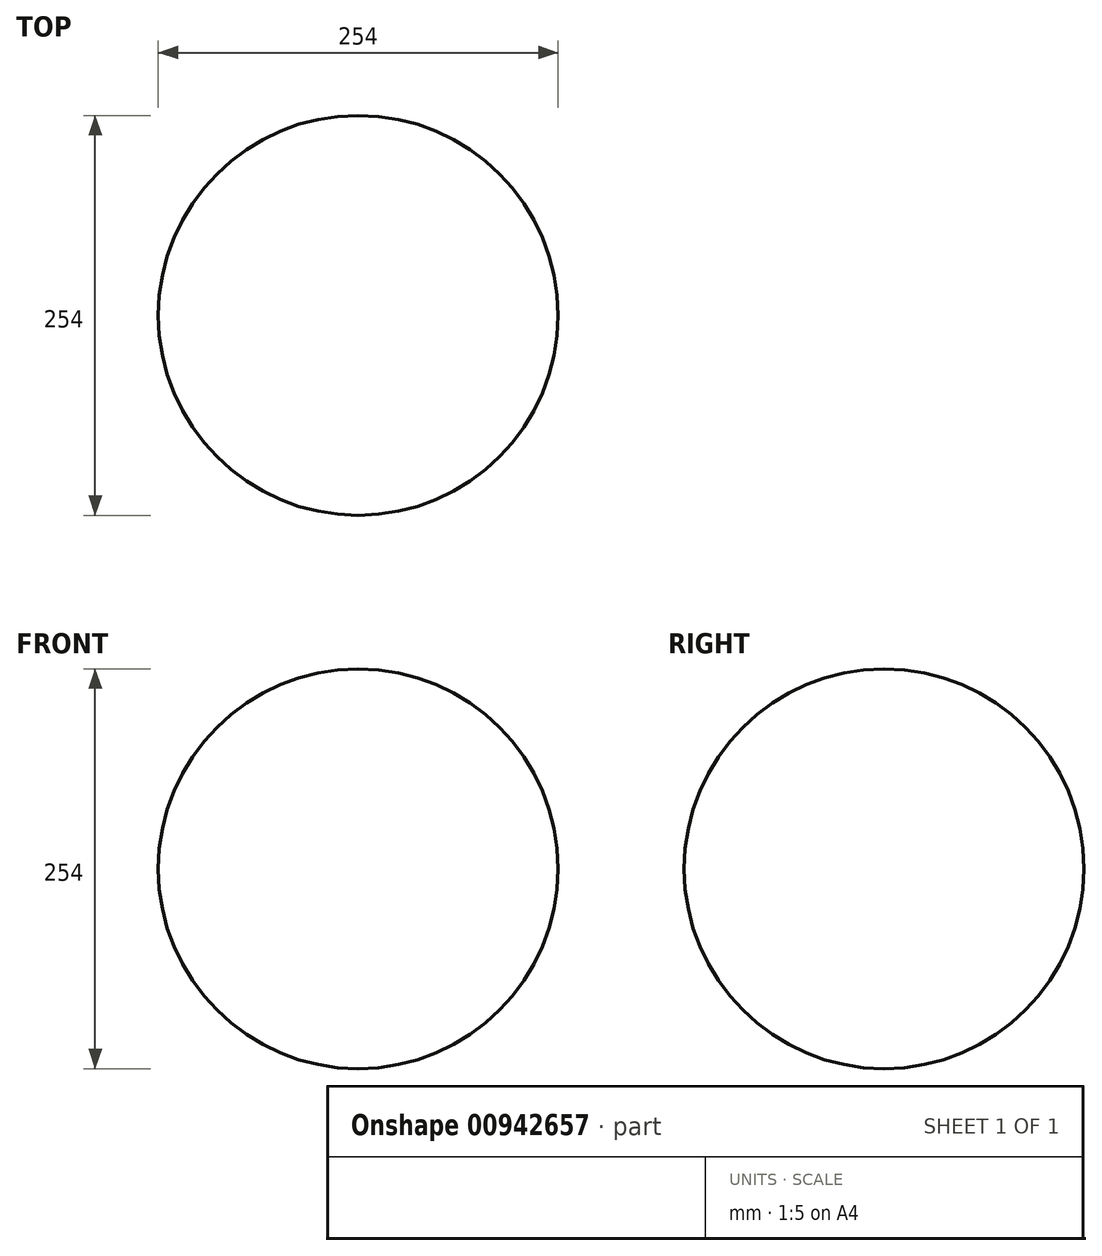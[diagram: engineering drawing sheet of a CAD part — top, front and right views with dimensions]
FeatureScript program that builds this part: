
annotation { "Feature Type Name" : "Feature", "Feature Type Description" : "" }
export const myFeature = defineFeature(function(context is Context, id is Id, definition is map)
    precondition{}
    {
        {
            var Q0;
            Q0=qCreatedBy(makeId("Right.planeOp"),FACE);
            var sketch = newSketch(context, id + "F0", { "sketchPlane" : qUnion([Q0])});
            skLineSegment(sketch, "E0", {"start": v(0, 127) * mm, "end": v(0, -127) * mm});
            skArc(sketch, "E1", {"start": v(0, -127) * mm, "mid": v(127, 0) * mm, "end": v(0, 127) * mm});
            skSolve(sketch);
        }
        {
            var Q0;
            Q0=makeQuery(id+"F0.imprint","IMPRINT",FACE,{"disambiguationData":[TD([[makeQuery(id+"F0.imprint","IMPRINT",EDGE,{"derivedFrom":sQuery(id+"F0.wireOp",EDGE,"E0")}),1.0]])]});
            var Q1;
            Q1=sQuery(id+"F0.wireOp",EDGE,"E0");
            revolve(context, id + "F1", {"surfaceOperationType" : NewSurfaceOperationType.NEW, "entities" : qUnion([Q0]), "axis" : qUnion([Q1]), "revolveType" : RevolveType.FULL});
        }
    });
